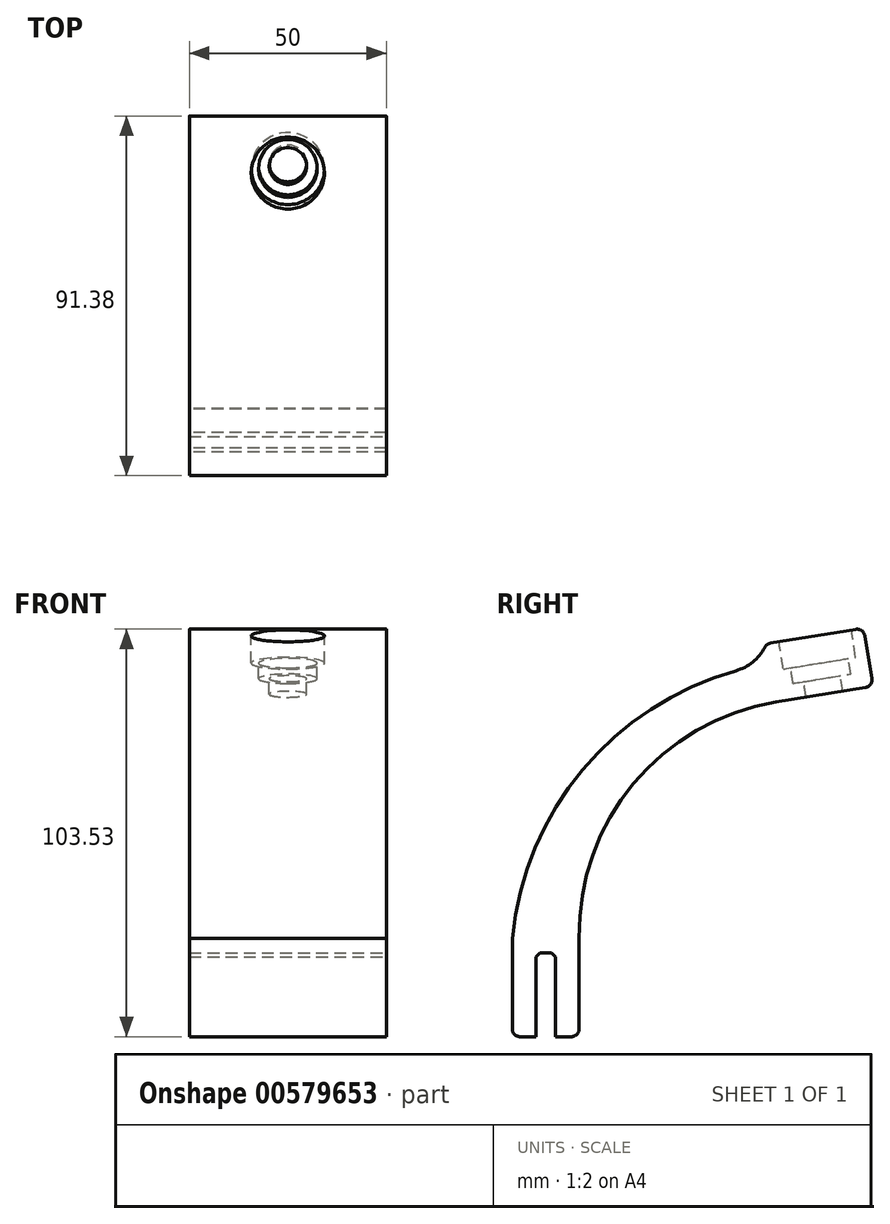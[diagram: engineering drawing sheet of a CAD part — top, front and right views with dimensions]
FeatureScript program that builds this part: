
annotation { "Feature Type Name" : "Feature", "Feature Type Description" : "" }
export const myFeature = defineFeature(function(context is Context, id is Id, definition is map)
    precondition{}
    {
        {
            var Q0;
            Q0=qCreatedBy(makeId("Right.planeOp"),FACE);
            var sketch = newSketch(context, id + "F0", { "sketchPlane" : qUnion([Q0])});
            skLineSegment(sketch, "E0", {"start": v(-36.82, -43.3) * mm, "end": v(-30.82, -43.3) * mm});
            skLineSegment(sketch, "E1", {"start": v(-30.82, -43.3) * mm, "end": v(-30.82, -22) * mm});
            skLineSegment(sketch, "E2", {"start": v(-30.82, -22) * mm, "end": v(-25.82, -22) * mm});
            skLineSegment(sketch, "E3", {"start": v(-25.82, -22) * mm, "end": v(-25.82, -43.3) * mm});
            skLineSegment(sketch, "E4", {"start": v(-25.82, -43.3) * mm, "end": v(-19.82, -43.3) * mm});
            skLineSegment(sketch, "E5", {"start": v(-19.82, -43.3) * mm, "end": v(-19.82, -18.3) * mm});
            skLineSegment(sketch, "E6", {"start": v(30.18, 41.7) * mm, "end": v(54.86, 45.72) * mm});
            skLineSegment(sketch, "E7", {"start": v(54.86, 45.72) * mm, "end": v(53.25, 55.59) * mm});
            skLineSegment(sketch, "E8", {"start": v(53.25, 55.59) * mm, "end": v(28.57, 51.57) * mm});
            skLineSegment(sketch, "E9", {"start": v(-36.82, -18.3) * mm, "end": v(-36.82, -18.3) * mm});
            skLineSegment(sketch, "E10", {"start": v(-36.82, -18.3) * mm, "end": v(-36.82, -43.3) * mm});
            skArc(sketch, "E11", {"start": v(28.57, 51.57) * mm, "mid": v(-16.03, 27.77) * mm, "end": v(-36.82, -18.3) * mm});
            skArc(sketch, "E12", {"start": v(30.18, 41.7) * mm, "mid": v(-6.02, 21.03) * mm, "end": v(-19.82, -18.3) * mm});
            skSolve(sketch);
        }
        {
            var Q0;
            Q0=makeQuery(id+"F0.imprint","IMPRINT",FACE,{"disambiguationData":[TD([[makeQuery(id+"F0.imprint","IMPRINT",EDGE,{"derivedFrom":sQuery(id+"F0.wireOp",EDGE,"E0")}),1.0]])]});
            var Q1;
            Q1 = qSketchRegion(id + "FElaW82ufLD2XNr_0", true);
            extrude(context, id + "F1", {"entities" : qUnion([Q0, Q1]), "depth" : 50 * mm, "offsetDistance" : 25 * mm});
        }
        {
            var Q0;
            Q0=makeQuery(id+"F1.opExtrude","SWEPT_FACE",FACE,{"disambiguationData":[OSD([sQuery(id+"F0.wireOp",EDGE,"E8")])]});
            extrude(context, id + "F2", {"entities" : qUnion([Q0]), "operationType" : NewBodyOperationType.ADD, "depth" : 5 * mm, "offsetDistance" : 25 * mm});
        }
        {
            var Q0;
            Q0=makeQuery(id+"F2.opExtrude","CAP_FACE",FACE,{"disambiguationData":[OSD([sQuery(id+"F0.wireOp",EDGE,"E8")])],"isStart":false});
            var sketch = newSketch(context, id + "F3", { "sketchPlane" : qUnion([Q0])});
            skCircle(sketch, "E13", {"center": v(25, 49) * mm, "radius": 4.74 * mm});
            skCircle(sketch, "E14", {"center": v(25, 49) * mm, "radius": 7.45 * mm});
            skSolve(sketch);
        }
        {
            var Q0;
            Q0=sQuery(id+"F3.wireOp",VERTEX,"E13.center");
            var Q1;
            Q1=makeQuery(id+"F1.opExtrude","SWEPT_BODY",BODY,{"disambiguationData":[OSD([sQuery(id+"F0.wireOp",EDGE,"E0"),sQuery(id+"F0.wireOp",EDGE,"E1"),sQuery(id+"F0.wireOp",EDGE,"E2"),sQuery(id+"F0.wireOp",EDGE,"E3"),sQuery(id+"F0.wireOp",EDGE,"E4"),sQuery(id+"F0.wireOp",EDGE,"E5"),sQuery(id+"F0.wireOp",EDGE,"E6"),sQuery(id+"F0.wireOp",EDGE,"E7"),sQuery(id+"F0.wireOp",EDGE,"E8"),sQuery(id+"F0.wireOp",EDGE,"E10"),sQuery(id+"F0.wireOp",EDGE,"E11"),sQuery(id+"F0.wireOp",EDGE,"E12")])]});
            hole(context, id + "F4", {"style" : HoleStyle.C_BORE, "endStyle" : HoleEndStyle.THROUGH, "holeDiameter" : 9.5 * mm, "cBoreDiameter" : 18.6 * mm, "cBoreDepth" : 7 * mm, "isTappedThrough" : true, "tappedDepth" : 12 * mm, "tapClearance" : 3, "locations" : qUnion([Q0]), "scope" : qUnion([Q1]), "majorDiameter" : 5 * mm});
        }
        {
            var Q0;
            {var subQ0=sQuery(id+"F0.wireOp",EDGE,"E11");var subQ1=sQuery(id+"F0.wireOp",EDGE,"E8");Q0=makeQuery(id+"F2.boolean.opBoolean","MERGE",EDGE,{"derivedFrom":[makeQuery(id+"F1.opExtrude","SWEPT_EDGE",EDGE,{"disambiguationData":[OSD([subQ1,subQ0])]}),makeQuery(id+"F2.opExtrude","CAP_EDGE",EDGE,{"disambiguationData":[OSD([subQ1,subQ0])],"isStart":true})]});}
            fillet(context, id + "F5", {"entities" : qUnion([Q0]), "radius" : 12 * mm, "tangentPropagation" : true, "allowEdgeOverflow" : false});
        }
        {
            var Q0;
            {var subQ0=sQuery(id+"F0.wireOp",EDGE,"E8");var subQ1=sQuery(id+"F0.wireOp",EDGE,"E11");Q0=makeQuery(id+"F5.opFillet","BLEND_EDGE",EDGE,{"blendedFrom":[makeQuery(id+"F2.boolean.opBoolean","MERGE",EDGE,{"derivedFrom":[makeQuery(id+"F1.opExtrude","SWEPT_EDGE",EDGE,{"disambiguationData":[OSD([subQ0,subQ1])]}),makeQuery(id+"F2.opExtrude","CAP_EDGE",EDGE,{"disambiguationData":[OSD([subQ0,subQ1])],"isStart":true})]}),makeQuery(id+"F2.opExtrude","CAP_FACE",FACE,{"disambiguationData":[OSD([subQ0])],"isStart":false})],"blendedInto":[makeQuery(id+"F2.opExtrude","CAP_FACE",FACE,{"disambiguationData":[OSD([subQ0])],"isStart":false})]});}
            fillet(context, id + "F6", {"entities" : qUnion([Q0]), "radius" : 2 * mm, "tangentPropagation" : true, "allowEdgeOverflow" : false});
        }
        {
            var Q0;
            Q0=makeQuery(id+"F2.opExtrude","CAP_EDGE",EDGE,{"disambiguationData":[OSD([sQuery(id+"F0.wireOp",EDGE,"E7"),sQuery(id+"F0.wireOp",EDGE,"E8")])],"isStart":false});
            fillet(context, id + "F7", {"entities" : qUnion([Q0]), "radius" : 2 * mm, "tangentPropagation" : true, "allowEdgeOverflow" : false});
        }
        {
            var Q0;
            Q0=makeQuery(id+"F1.opExtrude","SWEPT_EDGE",EDGE,{"disambiguationData":[OSD([sQuery(id+"F0.wireOp",EDGE,"E6"),sQuery(id+"F0.wireOp",EDGE,"E7")])]});
            fillet(context, id + "F8", {"entities" : qUnion([Q0]), "radius" : 2 * mm, "tangentPropagation" : true, "allowEdgeOverflow" : false});
        }
        {
            var Q0;
            Q0=makeQuery(id+"F1.opExtrude","SWEPT_EDGE",EDGE,{"disambiguationData":[OSD([sQuery(id+"F0.wireOp",EDGE,"E4"),sQuery(id+"F0.wireOp",EDGE,"E5")])]});
            fillet(context, id + "F9", {"entities" : qUnion([Q0]), "radius" : 2 * mm, "tangentPropagation" : true, "allowEdgeOverflow" : false});
        }
        {
            var Q0;
            Q0=makeQuery(id+"F1.opExtrude","SWEPT_EDGE",EDGE,{"disambiguationData":[OSD([sQuery(id+"F0.wireOp",EDGE,"E0"),sQuery(id+"F0.wireOp",EDGE,"E10")])]});
            fillet(context, id + "F10", {"entities" : qUnion([Q0]), "radius" : 2 * mm, "tangentPropagation" : true, "allowEdgeOverflow" : false});
        }
        {
            var Q0;
            Q0=makeQuery(id+"F1.opExtrude","SWEPT_EDGE",EDGE,{"disambiguationData":[OSD([sQuery(id+"F0.wireOp",EDGE,"E1"),sQuery(id+"F0.wireOp",EDGE,"E2")])]});
            chamfer(context, id + "F11", {"entities" : qUnion([Q0]), "width" : 1 * mm, "tangentPropagation" : true});
        }
        {
            var Q0;
            Q0=makeQuery(id+"F1.opExtrude","SWEPT_EDGE",EDGE,{"disambiguationData":[OSD([sQuery(id+"F0.wireOp",EDGE,"E2"),sQuery(id+"F0.wireOp",EDGE,"E3")])]});
            chamfer(context, id + "F12", {"entities" : qUnion([Q0]), "width" : 1 * mm, "tangentPropagation" : true});
        }
        {
            var Q0;
            Q0=makeQuery(id+"F3.imprint","IMPRINT",FACE,{"disambiguationData":[TD([[makeQuery(id+"F3.imprint","IMPRINT",EDGE,{"derivedFrom":sQuery(id+"F3.wireOp",EDGE,"E13")}),-1.0]])]});
            extrude(context, id + "F13", {"entities" : qUnion([Q0]), "operationType" : NewBodyOperationType.REMOVE, "oppositeDirection" : true, "depth" : 11 * mm, "offsetDistance" : 25 * mm});
        }
    });
